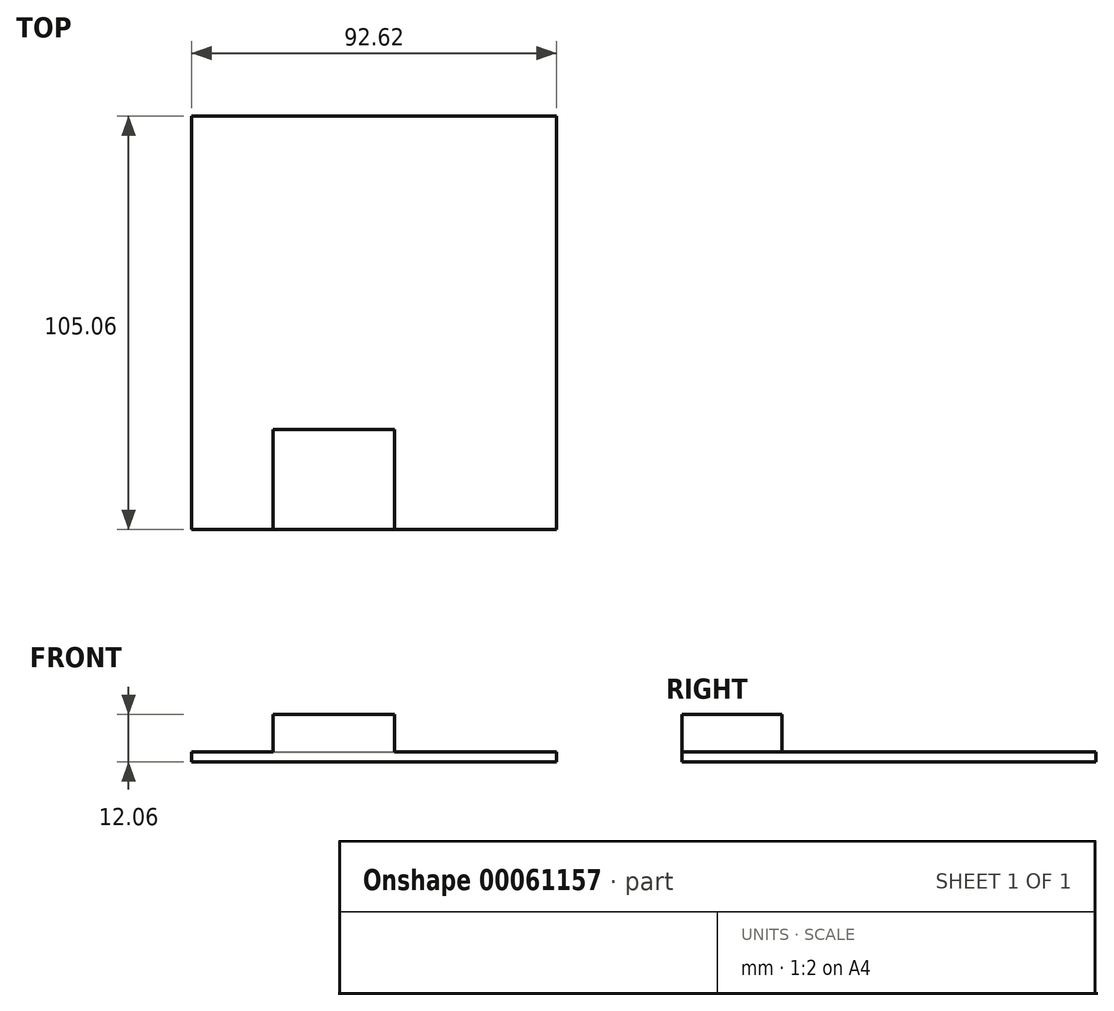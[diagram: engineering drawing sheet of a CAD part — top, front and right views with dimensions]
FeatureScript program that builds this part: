
annotation { "Feature Type Name" : "Feature", "Feature Type Description" : "" }
export const myFeature = defineFeature(function(context is Context, id is Id, definition is map)
    precondition{}
    {
        {
            var Q0;
            Q0=qCreatedBy(makeId("Top.planeOp"),FACE);
            var sketch = newSketch(context, id + "F0", { "sketchPlane" : qUnion([Q0])});
            skLineSegment(sketch, "E0.bottom", {"start": v(-55.67, -63.4) * mm, "end": v(36.95, -63.4) * mm});
            skLineSegment(sketch, "E0.top", {"start": v(-55.67, 41.67) * mm, "end": v(36.95, 41.67) * mm});
            skLineSegment(sketch, "E0.left", {"start": v(-55.67, -63.4) * mm, "end": v(-55.67, 41.67) * mm});
            skLineSegment(sketch, "E0.right", {"start": v(36.95, -63.4) * mm, "end": v(36.95, 41.67) * mm});
            skSolve(sketch);
        }
        {
            var Q0;
            Q0=makeQuery(id+"F0.imprint","IMPRINT",FACE,{"disambiguationData":[TD([[makeQuery(id+"F0.imprint","IMPRINT",EDGE,{"derivedFrom":sQuery(id+"F0.wireOp",EDGE,"E0.bottom")}),1.0]])]});
            extrude(context, id + "F1", {"entities" : qUnion([Q0]), "depth" : 2.54 * mm});
        }
        {
            var Q0;
            Q0=makeQuery(id+"F1.opExtrude","SWEPT_FACE",FACE,{"disambiguationData":[OSD([sQuery(id+"F0.wireOp",EDGE,"E0.bottom")])]});
            var sketch = newSketch(context, id + "F2", { "sketchPlane" : qUnion([Q0])});
            skLineSegment(sketch, "E1.bottom", {"start": v(-34.94, 2.54) * mm, "end": v(-4.16, 2.54) * mm});
            skLineSegment(sketch, "E1.top", {"start": v(-34.94, 12.06) * mm, "end": v(-4.16, 12.06) * mm});
            skLineSegment(sketch, "E1.left", {"start": v(-34.94, 2.54) * mm, "end": v(-34.94, 12.06) * mm});
            skLineSegment(sketch, "E1.right", {"start": v(-4.16, 2.54) * mm, "end": v(-4.16, 12.06) * mm});
            skSolve(sketch);
        }
        {
            var Q0;
            Q0=makeQuery(id+"F2.imprint","IMPRINT",FACE,{"disambiguationData":[TD([[makeQuery(id+"F2.imprint","IMPRINT",EDGE,{"derivedFrom":sQuery(id+"F2.wireOp",EDGE,"E1.bottom")}),1.0]])]});
            extrude(context, id + "F3", {"entities" : qUnion([Q0]), "operationType" : NewBodyOperationType.ADD, "oppositeDirection" : true, "depth" : 25.4 * mm});
        }
    });
